# Revit family: Kamstrup_Multical_602+Ultraflow 54 фланцевые
name_source: partatom
category: Арматура трубопроводов
revit_build: Autodesk Revit 2016 (Build: 20150714_1515(x64)
units: mm (PartAtom-declared; Revit-internal decimal feet)

## family parameters
Всегда вертикально = Да
На основе рабочей плоскости = Нет
Общий = Нет
При загрузке вырезать с полостями = Нет
Размер круглого соединителя = Использовать диаметр
Тип детали = Встроенный датчик

## types (1)
- Kamstrup_Multical_602+Ultraflow 54 фланцевые
    150 = 150 мм
    ID01 = 0 Без модуля верха
    ID02 = 2 Расчет дельты энергий + почасовой архив
    ID03 = 3 PQ или дельта t-ограничитель + почасовой архив
    ID04 = 5 Выход данных + почасовой архив
    ID05 = 7 M-BUS
    ID06 = 9 Расчет дельты объемов +почасовой архив
    ID07 = A 2 имп.выхода CE и CV + почасовой архив +расписание
    ID08 = B ЧРВ + 2 имп.выхода CE и CV + программируемый архив
    ID09 = C 2 имп.выхода CE и CV
    ID10 = 00 Без модуля низа
    ID11 = 10 Данные + импульсные входы
    ID12 = 20 M-Bus + импульсные входы
    ID13 = 21 Радио Роутер + импульсные входы
    ID14 = 22 Программируемый архив + ЧРВ + входы 4…20 мA + имп.Входы
    ID15 = 23 0/4…20 мA выходы : 23 4…20 мA выходы
    ID16 = 24 LonWorks + импульсные входы
    ID17 = 25 Радио + имп.входы (встроенная антенна) 434 или 444 МГц
    ID18 = 26 Радио + имп.входы (для внешней антенны) 434 или 444 МГц
    ID19 = 27 M-Bus с альтернативными регистрами + имп.входы
    ID20 = 28 M-Bus с пакетом данных M-size + имп.входы
    ID21 = 29 M-Bus с MC-III совместимым пакетом данных + имп.Входы
    ID22 = 30 Беспроводной M-Bus Mode C1 + 2 импульсных входа (VA, VB) (инд.ключ шифрования)
    ID23 = 31 Беспроводной M-Bus, Режим T1 OMS 15 мин. (инд.ключ)
    ID24 = 35 Беспроводной M-Bus Mode C1 с альт. регистр. + 2 имп. вх.(VA, VB)
    ID25 = 36 Беспроводной M-Bus, Режим T1 OMS 16 сек. (инд.ключ)
    ID26 = 38 Беспроводной M-Bus, C1, для стационарных сетей, (инд.ключ)
    ID27 = 39 Беспроводной M-Bus, C1, для стационарных сетей, (инд.ключ), PDO Data
    ID28 = 60 ZigBee 2.4 ГГц встроенная антенна + 2 имп.входа (VA, VB)
    ID29 = 62 Metasys N2 (RS485) + 2 импульсных входа (VA, VB)
    ID30 = 64 SIOX модуль (Автоматическое определение скорости)
    ID31 = 66 BACnetMS/TP + импульсный входы : 66  TP + импульсный входы
    ID32 = 67 Modbus RTU + импульсный входы
    ID33 = 2 Батарея, D-элемент
    ID34 = 7 230 В AC изолированный линейный
    ID35 = 8 24 В AC изолированный линейный
    ID36 = 00 Без датчика температуры
    ID37 = 0A Пара датчиков для гильз кабель 1,5 м
    ID38 = 0B Пара датчиков для гильз кабель 3,0 м
    ID39 = 0C Пара датчиков для гильз кабель 5 м
    ID40 = 0D Пара датчиков для гильз кабель 10 м
    ID41 = 0F Пара коротких датчиков прямого погружения кабель 1,5 м
    ID42 = 0G Пара коротких датчиков прямого погружения кабель 3,0 м
    ID43 = 0L Комплект из 3 датчиков для гильз кабель 1,5 м
    ID44 = Q3 Комплект из 3 коротких датчиков прям.погружения кабель 1,5 м
    ID45 = 7 Для одного ULTRAFLOW
    ID46 = 8 Для двух (одинаковых) ULTRAFLOW
    ID47 = 4 Теплосчетчик, национальная сертификация
    ID48 = 5 Счетчик энергии охлаждения (TS27.02+DK268)
    ID49 = 9 Счетчик энергии
    URL = https://www.kamstrup.com
    Адрес = 141008, Московская обл., г. Мытищи, ул. Колпакова, 26
    Изготовитель = ЗАО «Камструп»
    Таблица выбора = multical 602
    Таблица_выбора = ultraflow 54-602
    Телефон = +7 495 545 00 01

## geometry (parser evidence)
native form markers: Blend x12
no freeform markers — native parametric forms only
